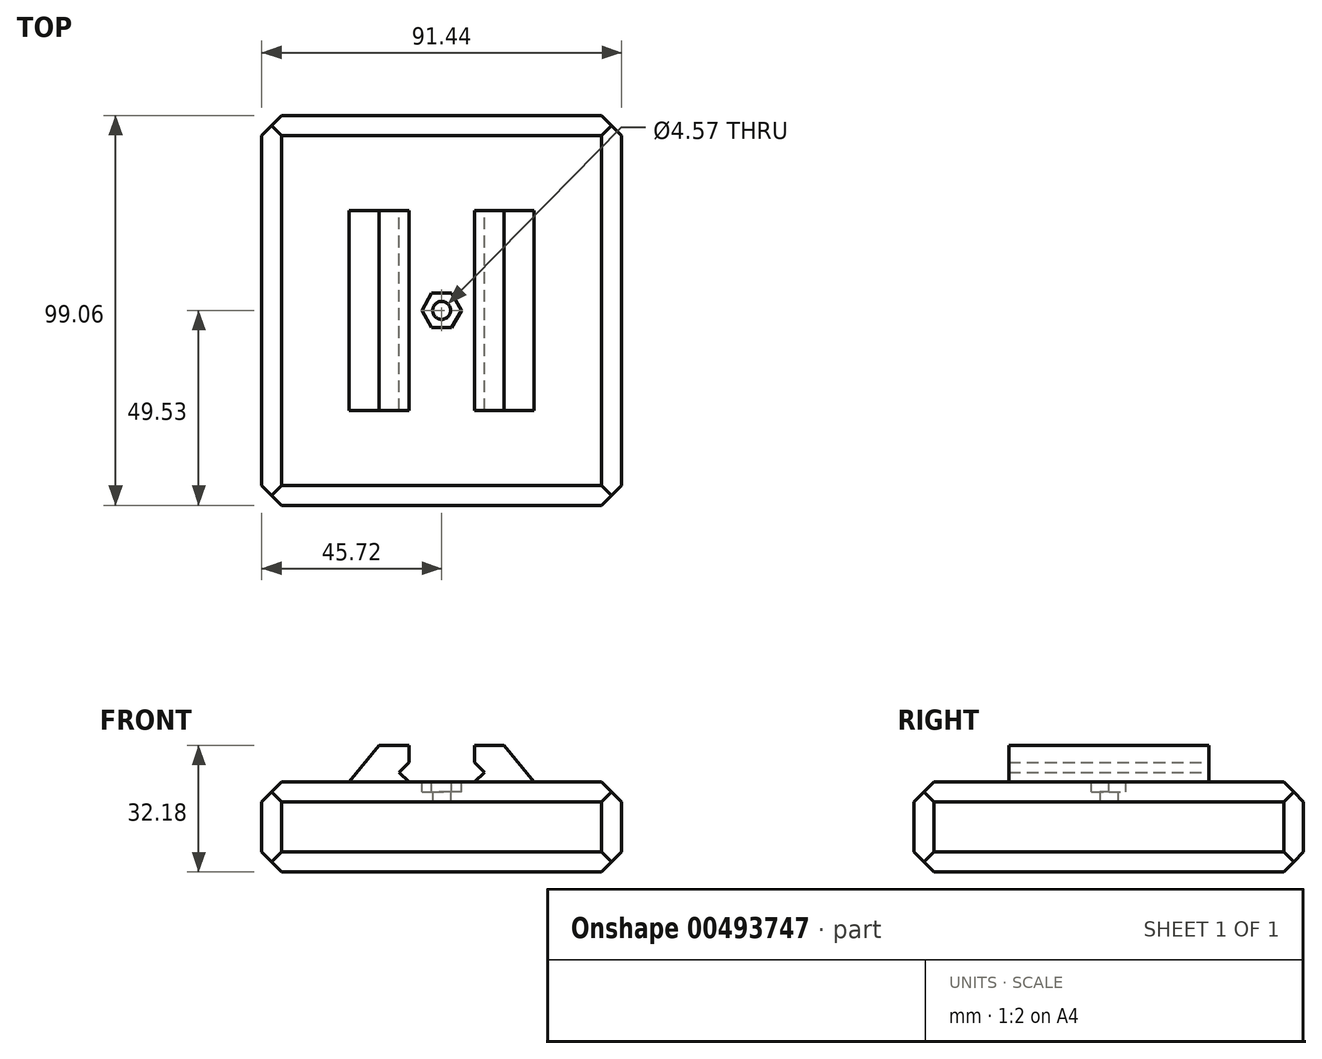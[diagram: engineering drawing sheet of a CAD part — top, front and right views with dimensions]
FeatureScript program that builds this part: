
annotation { "Feature Type Name" : "Feature", "Feature Type Description" : "" }
export const myFeature = defineFeature(function(context is Context, id is Id, definition is map)
    precondition{}
    {
        {
            var Q0;
            Q0=qCreatedBy(makeId("Top.planeOp"),FACE);
            var sketch = newSketch(context, id + "F0", { "sketchPlane" : qUnion([Q0])});
            skLineSegment(sketch, "E0.bottom", {"start": v(-40.64, 44.45) * mm, "end": v(40.64, 44.45) * mm});
            skLineSegment(sketch, "E0.top", {"start": v(-40.64, -44.45) * mm, "end": v(40.64, -44.45) * mm});
            skLineSegment(sketch, "E0.left", {"start": v(-40.64, 44.45) * mm, "end": v(-40.64, -44.45) * mm});
            skLineSegment(sketch, "E0.right", {"start": v(40.64, 44.45) * mm, "end": v(40.64, -44.45) * mm});
            skPoint(sketch, "E0.middle", {"position": v(0, 0) * mm});
            skLineSegment(sketch, "E1.0", {"start": v(-45.72, 49.53) * mm, "end": v(45.72, 49.53) * mm});
            skLineSegment(sketch, "E1.1", {"start": v(-45.72, 49.53) * mm, "end": v(-45.72, -49.53) * mm});
            skLineSegment(sketch, "E1.2", {"start": v(-45.72, -49.53) * mm, "end": v(45.72, -49.53) * mm});
            skLineSegment(sketch, "E1.3", {"start": v(45.72, 49.53) * mm, "end": v(45.72, -49.53) * mm});
            skSolve(sketch);
        }
        {
            var Q0;
            Q0 = qSketchRegion(id + "F0", true);
            extrude(context, id + "F1", {"entities" : qUnion([Q0]), "oppositeDirection" : true, "depth" : 17.78 * mm});
        }
        {
            var Q0;
            Q0=makeQuery(id+"F1.opExtrude","CAP_FACE",FACE,{"disambiguationData":[OSD([sQuery(id+"F0.wireOp",EDGE,"E0.bottom"),sQuery(id+"F0.wireOp",EDGE,"E0.top"),sQuery(id+"F0.wireOp",EDGE,"E0.left"),sQuery(id+"F0.wireOp",EDGE,"E0.right"),sQuery(id+"F0.wireOp",EDGE,"E1.0"),sQuery(id+"F0.wireOp",EDGE,"E1.1"),sQuery(id+"F0.wireOp",EDGE,"E1.2"),sQuery(id+"F0.wireOp",EDGE,"E1.3")])],"isStart":true});
            var sketch = newSketch(context, id + "F2", { "sketchPlane" : qUnion([Q0])});
            skLineSegment(sketch, "E2.0", {"start": v(-45.72, 49.53) * mm, "end": v(45.72, 49.53) * mm});
            skLineSegment(sketch, "E3.0", {"start": v(-45.72, 49.53) * mm, "end": v(-45.72, -49.53) * mm});
            skLineSegment(sketch, "E4.0", {"start": v(45.72, 49.53) * mm, "end": v(45.72, -49.53) * mm});
            skLineSegment(sketch, "E5.0", {"start": v(-45.72, -49.53) * mm, "end": v(45.72, -49.53) * mm});
            skSolve(sketch);
        }
        {
            var Q0;
            Q0 = qSketchRegion(id + "F2", true);
            extrude(context, id + "F3", {"entities" : qUnion([Q0]), "operationType" : NewBodyOperationType.ADD, "depth" : 5.08 * mm});
        }
        {
            var Q0;
            Q0=makeQuery(id+"F3.boolean.opBoolean","MERGE",EDGE,{"derivedFrom":[makeQuery(id+"F1.opExtrude","SWEPT_EDGE",EDGE,{"disambiguationData":[OSD([sQuery(id+"F0.wireOp",EDGE,"E1.0"),sQuery(id+"F0.wireOp",EDGE,"E1.1")])]}),makeQuery(id+"F3.opExtrude","SWEPT_EDGE",EDGE,{"disambiguationData":[OSD([sQuery(id+"F2.wireOp",EDGE,"E2.0"),sQuery(id+"F2.wireOp",EDGE,"E3.0")])]})]});
            var Q1;
            Q1=makeQuery(id+"F3.boolean.opBoolean","MERGE",EDGE,{"derivedFrom":[makeQuery(id+"F1.opExtrude","SWEPT_EDGE",EDGE,{"disambiguationData":[OSD([sQuery(id+"F0.wireOp",EDGE,"E1.0"),sQuery(id+"F0.wireOp",EDGE,"E1.3")])]}),makeQuery(id+"F3.opExtrude","SWEPT_EDGE",EDGE,{"disambiguationData":[OSD([sQuery(id+"F2.wireOp",EDGE,"E2.0"),sQuery(id+"F2.wireOp",EDGE,"E4.0")])]})]});
            var Q2;
            Q2=makeQuery(id+"F3.boolean.opBoolean","MERGE",EDGE,{"derivedFrom":[makeQuery(id+"F1.opExtrude","SWEPT_EDGE",EDGE,{"disambiguationData":[OSD([sQuery(id+"F0.wireOp",EDGE,"E1.2"),sQuery(id+"F0.wireOp",EDGE,"E1.3")])]}),makeQuery(id+"F3.opExtrude","SWEPT_EDGE",EDGE,{"disambiguationData":[OSD([sQuery(id+"F2.wireOp",EDGE,"E4.0"),sQuery(id+"F2.wireOp",EDGE,"E5.0")])]})]});
            var Q3;
            Q3=makeQuery(id+"F3.boolean.opBoolean","MERGE",EDGE,{"derivedFrom":[makeQuery(id+"F1.opExtrude","SWEPT_EDGE",EDGE,{"disambiguationData":[OSD([sQuery(id+"F0.wireOp",EDGE,"E1.1"),sQuery(id+"F0.wireOp",EDGE,"E1.2")])]}),makeQuery(id+"F3.opExtrude","SWEPT_EDGE",EDGE,{"disambiguationData":[OSD([sQuery(id+"F2.wireOp",EDGE,"E3.0"),sQuery(id+"F2.wireOp",EDGE,"E5.0")])]})]});
            chamfer(context, id + "F4", {"entities" : qUnion([Q0, Q1, Q2, Q3]), "width" : 5.08 * mm, "tangentPropagation" : true});
        }
        {
            var Q0;
            Q0=qCreatedBy(makeId("Front.planeOp"),FACE);
            var sketch = newSketch(context, id + "F5", { "sketchPlane" : qUnion([Q0])});
            skLineSegment(sketch, "E6.0", {"start": v(8.34, 5.08) * mm, "end": v(15.88, 5.08) * mm});
            skLineSegment(sketch, "E7", {"start": v(0, 5.08) * mm, "end": v(0, 20.95) * mm, "construction": true});
            skPoint(sketch, "E7.endSnap0", {"position": v(0, 5.08) * mm});
            skLineSegment(sketch, "E8", {"start": v(15.88, 14.4) * mm, "end": v(15.88, 5.08) * mm});
            skLineSegment(sketch, "E9", {"start": v(8.34, 5.08) * mm, "end": v(10.86, 7.6) * mm});
            skLineSegment(sketch, "E10", {"start": v(10.86, 7.6) * mm, "end": v(8.34, 10.1) * mm});
            skLineSegment(sketch, "E11", {"start": v(8.34, 10.1) * mm, "end": v(8.34, 14.4) * mm});
            skLineSegment(sketch, "E12", {"start": v(8.34, 14.4) * mm, "end": v(15.88, 14.4) * mm});
            skPoint(sketch, "E13.orphan", {"position": v(-40.64, 5.08) * mm});
            skPoint(sketch, "E14.orphan", {"position": v(40.64, 5.08) * mm});
            skLineSegment(sketch, "E15.MirrorCS", {"start": v(-8.34, 14.4) * mm, "end": v(-15.88, 14.4) * mm});
            skLineSegment(sketch, "E16.MirrorCS", {"start": v(-8.34, 10.1) * mm, "end": v(-8.34, 14.4) * mm});
            skLineSegment(sketch, "E17.MirrorCS", {"start": v(-10.86, 7.6) * mm, "end": v(-8.34, 10.1) * mm});
            skLineSegment(sketch, "E18.MirrorCS", {"start": v(-8.34, 5.08) * mm, "end": v(-10.86, 7.6) * mm});
            skLineSegment(sketch, "E19.MirrorCS", {"start": v(-8.34, 5.08) * mm, "end": v(-15.88, 5.08) * mm});
            skLineSegment(sketch, "E20.MirrorCS", {"start": v(-15.88, 14.4) * mm, "end": v(-15.88, 5.08) * mm});
            skSolve(sketch);
        }
        {
            var Q0;
            Q0 = qSketchRegion(id + "F5", true);
            extrude(context, id + "F6", {"entities" : qUnion([Q0]), "operationType" : NewBodyOperationType.ADD, "endBound" : BoundingType.SYMMETRIC, "depth" : 50.8 * mm});
        }
        {
            var Q0;
            Q0=makeQuery(id+"F3.opExtrude","CAP_FACE",FACE,{"disambiguationData":[OSD([sQuery(id+"F2.wireOp",EDGE,"E2.0"),sQuery(id+"F2.wireOp",EDGE,"E3.0"),sQuery(id+"F2.wireOp",EDGE,"E4.0"),sQuery(id+"F2.wireOp",EDGE,"E5.0")])],"isStart":true});
            var sketch = newSketch(context, id + "F7", { "sketchPlane" : qUnion([Q0])});
            skCircle(sketch, "E21", {"center": v(0, 0) * mm, "radius": 2.29 * mm});
            skSolve(sketch);
        }
        {
            var Q0;
            Q0 = qSketchRegion(id + "F7", true);
            extrude(context, id + "F8", {"entities" : qUnion([Q0]), "operationType" : NewBodyOperationType.REMOVE, "oppositeDirection" : true, "depth" : 25.4 * mm});
        }
        {
            var Q0;
            Q0=makeQuery(id+"F3.opExtrude","CAP_FACE",FACE,{"disambiguationData":[OSD([sQuery(id+"F2.wireOp",EDGE,"E2.0"),sQuery(id+"F2.wireOp",EDGE,"E3.0"),sQuery(id+"F2.wireOp",EDGE,"E4.0"),sQuery(id+"F2.wireOp",EDGE,"E5.0")])],"isStart":false});
            var sketch = newSketch(context, id + "F9", { "sketchPlane" : qUnion([Q0])});
            skCircle(sketch, "E22.cCircle", {"center": v(0, 0) * mm, "radius": 4.37 * mm, "construction": true});
            skLineSegment(sketch, "E22.0", {"start": v(-2.52, 4.37) * mm, "end": v(2.52, 4.37) * mm});
            skLineSegment(sketch, "E22.1", {"start": v(2.52, 4.37) * mm, "end": v(5.04, 0) * mm});
            skLineSegment(sketch, "E22.2", {"start": v(5.04, 0) * mm, "end": v(2.52, -4.37) * mm});
            skLineSegment(sketch, "E22.3", {"start": v(2.52, -4.37) * mm, "end": v(-2.52, -4.37) * mm});
            skLineSegment(sketch, "E22.4", {"start": v(-2.52, -4.37) * mm, "end": v(-5.04, 0) * mm});
            skLineSegment(sketch, "E22.5", {"start": v(-5.04, 0) * mm, "end": v(-2.52, 4.37) * mm});
            skPoint(sketch, "E22.0.midPoint", {"position": v(0, 4.37) * mm});
            skSolve(sketch);
        }
        {
            var Q0;
            Q0 = qSketchRegion(id + "F9", true);
            extrude(context, id + "F10", {"entities" : qUnion([Q0]), "operationType" : NewBodyOperationType.REMOVE, "oppositeDirection" : true, "depth" : 2.54 * mm});
        }
        {
            var Q0;
            Q0=makeQuery(id+"F1.opExtrude","CAP_EDGE",EDGE,{"disambiguationData":[OSD([sQuery(id+"F0.wireOp",EDGE,"E1.0")])],"isStart":false});
            var Q1;
            Q1=makeQuery(id+"F1.opExtrude","CAP_EDGE",EDGE,{"disambiguationData":[OSD([sQuery(id+"F0.wireOp",EDGE,"E1.1")])],"isStart":false});
            var Q2;
            Q2=makeQuery(id+"F1.opExtrude","CAP_EDGE",EDGE,{"disambiguationData":[OSD([sQuery(id+"F0.wireOp",EDGE,"E1.2")])],"isStart":false});
            var Q3;
            Q3=makeQuery(id+"F1.opExtrude","CAP_EDGE",EDGE,{"disambiguationData":[OSD([sQuery(id+"F0.wireOp",EDGE,"E1.3")])],"isStart":false});
            var Q4;
            Q4=makeQuery(id+"F3.opExtrude","CAP_EDGE",EDGE,{"disambiguationData":[OSD([sQuery(id+"F2.wireOp",EDGE,"E2.0")])],"isStart":false});
            var Q5;
            Q5=makeQuery(id+"F3.opExtrude","CAP_EDGE",EDGE,{"disambiguationData":[OSD([sQuery(id+"F2.wireOp",EDGE,"E3.0")])],"isStart":false});
            var Q6;
            Q6=makeQuery(id+"F3.opExtrude","CAP_EDGE",EDGE,{"disambiguationData":[OSD([sQuery(id+"F2.wireOp",EDGE,"E5.0")])],"isStart":false});
            var Q7;
            Q7=makeQuery(id+"F3.opExtrude","CAP_EDGE",EDGE,{"disambiguationData":[OSD([sQuery(id+"F2.wireOp",EDGE,"E4.0")])],"isStart":false});
            chamfer(context, id + "F11", {"entities" : qUnion([Q0, Q1, Q2, Q3, Q4, Q5, Q6, Q7]), "width" : 5.08 * mm, "tangentPropagation" : true});
        }
        {
            var Q0;
            Q0=makeQuery(id+"F6.opExtrude","CAP_FACE",FACE,{"disambiguationData":[OSD([sQuery(id+"F5.wireOp",EDGE,"E6.0"),sQuery(id+"F5.wireOp",EDGE,"E8"),sQuery(id+"F5.wireOp",EDGE,"E9"),sQuery(id+"F5.wireOp",EDGE,"E10"),sQuery(id+"F5.wireOp",EDGE,"E11"),sQuery(id+"F5.wireOp",EDGE,"E12")])],"isStart":false});
            var sketch = newSketch(context, id + "F12", { "sketchPlane" : qUnion([Q0])});
            skLineSegment(sketch, "E23.0", {"start": v(-23.5, 5.08) * mm, "end": v(-15.88, 5.08) * mm});
            skLineSegment(sketch, "E24.0", {"start": v(-15.88, 14.4) * mm, "end": v(-15.88, 5.08) * mm});
            skLineSegment(sketch, "E25", {"start": v(-15.88, 14.4) * mm, "end": v(-23.5, 5.08) * mm});
            skPoint(sketch, "E26.0.end.orphan", {"position": v(15.88, 5.08) * mm});
            skPoint(sketch, "E26.0.start.orphan", {"position": v(15.88, 14.4) * mm});
            skPoint(sketch, "E27.orphan", {"position": v(40.64, 5.08) * mm});
            skPoint(sketch, "E28.orphan", {"position": v(-40.64, 5.08) * mm});
            skLineSegment(sketch, "E29.MirrorCS", {"start": v(15.88, 14.4) * mm, "end": v(15.88, 5.08) * mm});
            skLineSegment(sketch, "E30.MirrorCS", {"start": v(15.88, 14.4) * mm, "end": v(23.5, 5.08) * mm});
            skLineSegment(sketch, "E31.MirrorCS", {"start": v(23.5, 5.08) * mm, "end": v(15.88, 5.08) * mm});
            skSolve(sketch);
        }
        {
            var Q0;
            Q0 = qSketchRegion(id + "F12", true);
            var Q1;
            Q1=makeQuery(id+"F6.opExtrude","CAP_FACE",FACE,{"disambiguationData":[OSD([sQuery(id+"F5.wireOp",EDGE,"E6.0"),sQuery(id+"F5.wireOp",EDGE,"E8"),sQuery(id+"F5.wireOp",EDGE,"E9"),sQuery(id+"F5.wireOp",EDGE,"E10"),sQuery(id+"F5.wireOp",EDGE,"E11"),sQuery(id+"F5.wireOp",EDGE,"E12")])],"isStart":true});
            extrude(context, id + "F13", {"entities" : qUnion([Q0]), "operationType" : NewBodyOperationType.ADD, "endBound" : BoundingType.UP_TO_SURFACE, "oppositeDirection" : true, "endBoundEntityFace" : qUnion([Q1]), "depth" : 25.4 * mm});
        }
    });
